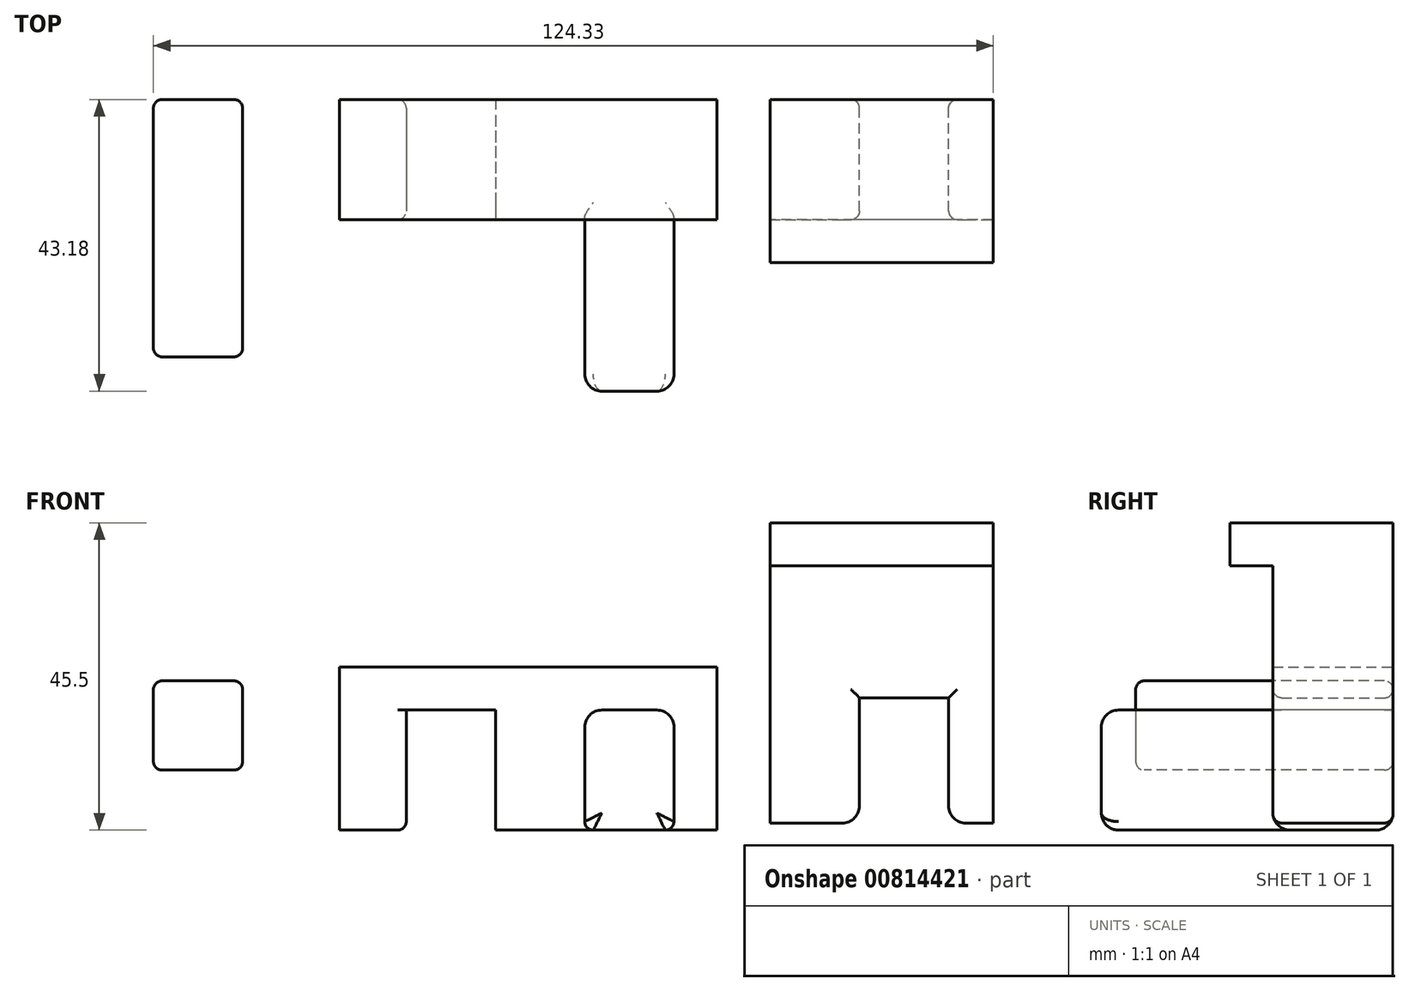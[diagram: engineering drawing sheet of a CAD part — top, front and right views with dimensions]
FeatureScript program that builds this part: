
annotation { "Feature Type Name" : "Feature", "Feature Type Description" : "" }
export const myFeature = defineFeature(function(context is Context, id is Id, definition is map)
    precondition{}
    {
        {
            var Q0;
            Q0=qCreatedBy(makeId("Front.planeOp"),FACE);
            var sketch = newSketch(context, id + "F0", { "sketchPlane" : qUnion([Q0])});
            skLineSegment(sketch, "E0.bottom", {"start": v(27.94, 8.9) * mm, "end": v(-27.94, 8.9) * mm});
            skLineSegment(sketch, "E0.top", {"start": v(27.94, -8.9) * mm, "end": v(-27.94, -8.9) * mm});
            skLineSegment(sketch, "E0.left", {"start": v(27.94, 8.9) * mm, "end": v(27.94, -8.9) * mm});
            skLineSegment(sketch, "E0.right", {"start": v(-27.94, 8.9) * mm, "end": v(-27.94, -8.9) * mm});
            skPoint(sketch, "E0.middle", {"position": v(0, 0) * mm});
            skSolve(sketch);
        }
        {
            var Q0;
            Q0=makeQuery(id+"F0.imprint","IMPRINT",FACE,{"disambiguationData":[TD([[makeQuery(id+"F0.imprint","IMPRINT",EDGE,{"derivedFrom":sQuery(id+"F0.wireOp",EDGE,"E0.bottom")}),1.0]])]});
            extrude(context, id + "F1", {"entities" : qUnion([Q0]), "depth" : 17.78 * mm, "offsetDistance" : 25.4 * mm});
        }
        {
            var Q0;
            Q0=makeQuery(id+"F1.opExtrude","CAP_FACE",FACE,{"disambiguationData":[OSD([sQuery(id+"F0.wireOp",EDGE,"E0.bottom"),sQuery(id+"F0.wireOp",EDGE,"E0.top"),sQuery(id+"F0.wireOp",EDGE,"E0.left"),sQuery(id+"F0.wireOp",EDGE,"E0.right")])],"isStart":false});
            var sketch = newSketch(context, id + "F2", { "sketchPlane" : qUnion([Q0])});
            skLineSegment(sketch, "E1.bottom", {"start": v(-18.03, 8.9) * mm, "end": v(-4.83, 8.9) * mm});
            skLineSegment(sketch, "E1.top", {"start": v(-18.03, -8.9) * mm, "end": v(-4.83, -8.9) * mm});
            skLineSegment(sketch, "E1.left", {"start": v(-18.03, 8.9) * mm, "end": v(-18.03, -8.9) * mm});
            skLineSegment(sketch, "E1.right", {"start": v(-4.83, 8.9) * mm, "end": v(-4.83, -8.9) * mm});
            skLineSegment(sketch, "E2.bottom", {"start": v(21.59, 8.9) * mm, "end": v(8.38, 8.9) * mm});
            skLineSegment(sketch, "E2.top", {"start": v(21.6, -8.9) * mm, "end": v(8.38, -8.9) * mm});
            skLineSegment(sketch, "E2.left", {"start": v(21.59, 8.9) * mm, "end": v(21.6, -8.9) * mm});
            skLineSegment(sketch, "E2.right", {"start": v(8.38, 8.9) * mm, "end": v(8.38, -8.9) * mm});
            skSolve(sketch);
        }
        {
            var Q0;
            Q0=makeQuery(id+"F2.imprint","IMPRINT",FACE,{"disambiguationData":[TD([[makeQuery(id+"F2.imprint","IMPRINT",EDGE,{"derivedFrom":sQuery(id+"F2.wireOp",EDGE,"E2.bottom")}),1.0]])]});
            extrude(context, id + "F3", {"entities" : qUnion([Q0]), "operationType" : NewBodyOperationType.ADD, "depth" : 25.4 * mm, "offsetDistance" : 25.4 * mm});
        }
        {
            var Q0;
            Q0=makeQuery(id+"F2.imprint","IMPRINT",FACE,{"disambiguationData":[TD([[makeQuery(id+"F2.imprint","IMPRINT",EDGE,{"derivedFrom":sQuery(id+"F2.wireOp",EDGE,"E1.bottom")}),1.0]])]});
            extrude(context, id + "F4", {"entities" : qUnion([Q0]), "operationType" : NewBodyOperationType.REMOVE, "endBound" : BoundingType.UP_TO_NEXT, "oppositeDirection" : true, "depth" : 25.4 * mm, "offsetDistance" : 25.4 * mm});
        }
        {
            var Q0;
            {var subQ2=sQuery(id+"F2.wireOp",EDGE,"E2.bottom");var subQ3=sQuery(id+"F0.wireOp",EDGE,"E0.left");var subQ6=sQuery(id+"F0.wireOp",EDGE,"E0.bottom");Q0=makeQuery(id+"F4.boolean.opBoolean","SPLIT",FACE,{"disambiguationData":[TD([makeQuery(id+"F1.opExtrude","SWEPT_FACE",FACE,{"disambiguationData":[OSD([subQ3])]})])],"derivedFrom":makeQuery(id+"F3.boolean.opBoolean","MERGE",FACE,{"derivedFrom":[makeQuery(id+"F1.opExtrude","SWEPT_FACE",FACE,{"disambiguationData":[OSD([subQ6])]}),makeQuery(id+"F3.opExtrude","SWEPT_FACE",FACE,{"disambiguationData":[OSD([subQ2])]})]})});}
            var sketch = newSketch(context, id + "F5", { "sketchPlane" : qUnion([Q0])});
            skLineSegment(sketch, "E3.bottom", {"start": v(27.94, 0) * mm, "end": v(-27.94, 0) * mm});
            skLineSegment(sketch, "E3.top", {"start": v(27.94, -17.78) * mm, "end": v(-27.94, -17.78) * mm});
            skLineSegment(sketch, "E3.left", {"start": v(27.94, 0) * mm, "end": v(27.94, -17.78) * mm});
            skLineSegment(sketch, "E3.right", {"start": v(-27.94, 0) * mm, "end": v(-27.94, -17.78) * mm});
            skSolve(sketch);
        }
        {
            var Q0;
            {var subQ6=sQuery(id+"F5.wireOp",EDGE,"E3.left");Q0=makeQuery(id+"F5.imprint","IMPRINT",FACE,{"disambiguationData":[TD([[makeQuery(id+"F5.imprint","IMPRINT",EDGE,{"derivedFrom":subQ6}),1.0]])]});}
            var Q1;
            {var subQ2=sQuery(id+"F5.wireOp",EDGE,"E3.right");Q1=makeQuery(id+"F5.imprint","IMPRINT",FACE,{"disambiguationData":[TD([[makeQuery(id+"F5.imprint","IMPRINT",EDGE,{"derivedFrom":subQ2}),1.0]])]});}
            extrude(context, id + "F6", {"entities" : qUnion([Q0, Q1]), "operationType" : NewBodyOperationType.ADD, "depth" : 6.35 * mm, "offsetDistance" : 25.4 * mm});
        }
        {
            var Q0;
            Q0=makeQuery(id+"F3.opExtrude","SWEPT_EDGE",EDGE,{"disambiguationData":[OSD([sQuery(id+"F0.wireOp",EDGE,"E0.bottom"),sQuery(id+"F2.wireOp",EDGE,"E2.bottom"),sQuery(id+"F2.wireOp",EDGE,"E2.left")])]});
            var Q1;
            Q1=makeQuery(id+"F3.opExtrude","CAP_EDGE",EDGE,{"disambiguationData":[OSD([sQuery(id+"F2.wireOp",EDGE,"E2.bottom")])],"isStart":false});
            var Q2;
            Q2=makeQuery(id+"F3.opExtrude","SWEPT_EDGE",EDGE,{"disambiguationData":[OSD([sQuery(id+"F0.wireOp",EDGE,"E0.bottom"),sQuery(id+"F2.wireOp",EDGE,"E2.bottom"),sQuery(id+"F2.wireOp",EDGE,"E2.right")])]});
            var Q3;
            Q3=makeQuery(id+"F3.opExtrude","CAP_EDGE",EDGE,{"disambiguationData":[OSD([sQuery(id+"F2.wireOp",EDGE,"E2.right")])],"isStart":false});
            var Q4;
            Q4=makeQuery(id+"F3.opExtrude","CAP_EDGE",EDGE,{"disambiguationData":[OSD([sQuery(id+"F2.wireOp",EDGE,"E2.left")])],"isStart":false});
            var Q5;
            Q5=makeQuery(id+"F3.opExtrude","CAP_EDGE",EDGE,{"disambiguationData":[OSD([sQuery(id+"F2.wireOp",EDGE,"E2.top")])],"isStart":false});
            var Q6;
            {var subQ1=makeQuery(id+"F3.opExtrude","SWEPT_FACE",FACE,{"disambiguationData":[OSD([sQuery(id+"F2.wireOp",EDGE,"E2.right")])]});var subQ2=sQuery(id+"F0.wireOp",EDGE,"E0.top");var subQ4=sQuery(id+"F0.wireOp",EDGE,"E0.right");Q6=makeQuery(id+"F4.boolean.opBoolean","SPLIT",EDGE,{"disambiguationData":[TD([subQ1])],"derivedFrom":makeQuery(id+"F3.boolean.opBoolean","SPLIT",EDGE,{"disambiguationData":[TD([makeQuery(id+"F1.opExtrude","SWEPT_FACE",FACE,{"disambiguationData":[OSD([subQ4])]})])],"derivedFrom":makeQuery(id+"F1.opExtrude","CAP_EDGE",EDGE,{"disambiguationData":[OSD([subQ2])],"isStart":false})})});}
            var Q7;
            {var subQ0=sQuery(id+"F0.wireOp",EDGE,"E0.left");var subQ1=sQuery(id+"F0.wireOp",EDGE,"E0.top");Q7=makeQuery(id+"F3.boolean.opBoolean","SPLIT",EDGE,{"disambiguationData":[TD([makeQuery(id+"F1.opExtrude","SWEPT_FACE",FACE,{"disambiguationData":[OSD([subQ0])]})])],"derivedFrom":makeQuery(id+"F1.opExtrude","CAP_EDGE",EDGE,{"disambiguationData":[OSD([subQ1])],"isStart":false})});}
            var Q8;
            {var subQ1=sQuery(id+"F0.wireOp",EDGE,"E0.right");var subQ2=makeQuery(id+"F1.opExtrude","SWEPT_FACE",FACE,{"disambiguationData":[OSD([subQ1])]});var subQ3=sQuery(id+"F0.wireOp",EDGE,"E0.top");Q8=makeQuery(id+"F4.boolean.opBoolean","SPLIT",EDGE,{"disambiguationData":[TD([subQ2])],"derivedFrom":makeQuery(id+"F3.boolean.opBoolean","SPLIT",EDGE,{"disambiguationData":[TD([subQ2])],"derivedFrom":makeQuery(id+"F1.opExtrude","CAP_EDGE",EDGE,{"disambiguationData":[OSD([subQ3])],"isStart":false})})});}
            var Q9;
            {var subQ0=sQuery(id+"F0.wireOp",EDGE,"E0.left");var subQ1=sQuery(id+"F0.wireOp",EDGE,"E0.top");Q9=makeQuery(id+"F4.boolean.opBoolean","SPLIT",EDGE,{"disambiguationData":[TD([makeQuery(id+"F1.opExtrude","SWEPT_FACE",FACE,{"disambiguationData":[OSD([subQ0])]})])],"derivedFrom":makeQuery(id+"F1.opExtrude","CAP_EDGE",EDGE,{"disambiguationData":[OSD([subQ1])],"isStart":true})});}
            var Q10;
            {var subQ0=sQuery(id+"F0.wireOp",EDGE,"E0.right");var subQ1=sQuery(id+"F0.wireOp",EDGE,"E0.top");Q10=makeQuery(id+"F4.boolean.opBoolean","SPLIT",EDGE,{"disambiguationData":[TD([makeQuery(id+"F1.opExtrude","SWEPT_FACE",FACE,{"disambiguationData":[OSD([subQ0])]})])],"derivedFrom":makeQuery(id+"F1.opExtrude","CAP_EDGE",EDGE,{"disambiguationData":[OSD([subQ1])],"isStart":true})});}
            fillet(context, id + "F7", {"entities" : qUnion([Q0, Q1, Q2, Q3, Q4, Q5, Q6, Q7, Q8, Q9, Q10]), "radius" : 2.54 * mm, "tangentPropagation" : true, "allowEdgeOverflow" : false});
        }
        {
            var Q0;
            Q0=qCreatedBy(makeId("Top.planeOp"),FACE);
            var sketch = newSketch(context, id + "F8", { "sketchPlane" : qUnion([Q0])});
            skLineSegment(sketch, "E4.bottom", {"start": v(-55.47, 0) * mm, "end": v(-42.26, 0) * mm});
            skLineSegment(sketch, "E4.top", {"start": v(-55.47, -38.1) * mm, "end": v(-42.26, -38.1) * mm});
            skLineSegment(sketch, "E4.left", {"start": v(-55.47, 0) * mm, "end": v(-55.47, -38.1) * mm});
            skLineSegment(sketch, "E4.right", {"start": v(-42.26, 0) * mm, "end": v(-42.26, -38.1) * mm});
            skSolve(sketch);
        }
        {
            var Q0;
            Q0=makeQuery(id+"F8.imprint","IMPRINT",FACE,{"disambiguationData":[TD([[makeQuery(id+"F8.imprint","IMPRINT",EDGE,{"derivedFrom":sQuery(id+"F8.wireOp",EDGE,"E4.bottom")}),-1.0]])]});
            extrude(context, id + "F9", {"entities" : qUnion([Q0]), "depth" : 13.2 * mm, "offsetDistance" : 25.4 * mm});
        }
        {
            var Q0;
            Q0=makeQuery(id+"F9.opExtrude","CAP_EDGE",EDGE,{"disambiguationData":[OSD([sQuery(id+"F8.wireOp",EDGE,"E4.left")])],"isStart":false});
            var Q1;
            Q1=makeQuery(id+"F9.opExtrude","CAP_EDGE",EDGE,{"disambiguationData":[OSD([sQuery(id+"F8.wireOp",EDGE,"E4.right")])],"isStart":true});
            var Q2;
            Q2=makeQuery(id+"F9.opExtrude","CAP_EDGE",EDGE,{"disambiguationData":[OSD([sQuery(id+"F8.wireOp",EDGE,"E4.right")])],"isStart":false});
            var Q3;
            Q3=makeQuery(id+"F9.opExtrude","CAP_EDGE",EDGE,{"disambiguationData":[OSD([sQuery(id+"F8.wireOp",EDGE,"E4.left")])],"isStart":true});
            var Q4;
            Q4=makeQuery(id+"F9.opExtrude","SWEPT_FACE",FACE,{"disambiguationData":[OSD([sQuery(id+"F8.wireOp",EDGE,"E4.top")])]});
            var Q5;
            Q5=makeQuery(id+"F9.opExtrude","SWEPT_FACE",FACE,{"disambiguationData":[OSD([sQuery(id+"F8.wireOp",EDGE,"E4.bottom")])]});
            fillet(context, id + "F10", {"entities" : qUnion([Q0, Q1, Q2, Q3, Q4, Q5]), "radius" : 1.27 * mm, "tangentPropagation" : true, "allowEdgeOverflow" : false});
        }
        {
            var Q0;
            Q0=qCreatedBy(makeId("Front.planeOp"),FACE);
            var sketch = newSketch(context, id + "F11", { "sketchPlane" : qUnion([Q0])});
            skLineSegment(sketch, "E5.bottom", {"start": v(35.84, 36.6) * mm, "end": v(68.86, 36.6) * mm});
            skLineSegment(sketch, "E5.top", {"start": v(35.84, -7.84) * mm, "end": v(68.86, -7.84) * mm});
            skLineSegment(sketch, "E5.left", {"start": v(35.84, 36.6) * mm, "end": v(35.84, -7.84) * mm});
            skLineSegment(sketch, "E5.right", {"start": v(68.86, 36.6) * mm, "end": v(68.86, -7.84) * mm});
            skLineSegment(sketch, "E6.bottom", {"start": v(62.25, -7.84) * mm, "end": v(49.04, -7.84) * mm});
            skLineSegment(sketch, "E6.top", {"start": v(62.25, 10.7) * mm, "end": v(49.04, 10.7) * mm});
            skLineSegment(sketch, "E6.left", {"start": v(62.25, -7.84) * mm, "end": v(62.25, 10.7) * mm});
            skLineSegment(sketch, "E6.right", {"start": v(49.04, -7.84) * mm, "end": v(49.04, 10.7) * mm});
            skSolve(sketch);
        }
        {
            var Q0;
            Q0=makeQuery(id+"F11.imprint","IMPRINT",FACE,{"disambiguationData":[TD([[makeQuery(id+"F11.imprint","IMPRINT",EDGE,{"derivedFrom":sQuery(id+"F11.wireOp",EDGE,"E5.bottom")}),-1.0]])]});
            extrude(context, id + "F12", {"entities" : qUnion([Q0]), "depth" : 17.78 * mm, "offsetDistance" : 25.4 * mm});
        }
        {
            var Q0;
            Q0=makeQuery(id+"F12.opExtrude","SWEPT_EDGE",EDGE,{"disambiguationData":[OSD([sQuery(id+"F11.wireOp",EDGE,"E5.top"),sQuery(id+"F11.wireOp",EDGE,"E6.bottom"),sQuery(id+"F11.wireOp",EDGE,"E6.right")])]});
            var Q1;
            Q1=makeQuery(id+"F12.opExtrude","SWEPT_EDGE",EDGE,{"disambiguationData":[OSD([sQuery(id+"F11.wireOp",EDGE,"E5.top"),sQuery(id+"F11.wireOp",EDGE,"E6.bottom"),sQuery(id+"F11.wireOp",EDGE,"E6.left")])]});
            fillet(context, id + "F13", {"entities" : qUnion([Q0, Q1]), "radius" : 2.54 * mm, "tangentPropagation" : true, "allowEdgeOverflow" : false});
        }
        {
            var Q0;
            Q0=makeQuery(id+"F12.opExtrude","CAP_FACE",FACE,{"disambiguationData":[OSD([sQuery(id+"F11.wireOp",EDGE,"E5.bottom"),sQuery(id+"F11.wireOp",EDGE,"E5.top"),sQuery(id+"F11.wireOp",EDGE,"E5.left"),sQuery(id+"F11.wireOp",EDGE,"E5.right"),sQuery(id+"F11.wireOp",EDGE,"E6.top"),sQuery(id+"F11.wireOp",EDGE,"E6.left"),sQuery(id+"F11.wireOp",EDGE,"E6.right")])],"isStart":false});
            var sketch = newSketch(context, id + "F14", { "sketchPlane" : qUnion([Q0])});
            skLineSegment(sketch, "E7.bottom", {"start": v(68.86, 36.6) * mm, "end": v(35.84, 36.6) * mm});
            skLineSegment(sketch, "E7.top", {"start": v(68.86, 30.26) * mm, "end": v(35.84, 30.26) * mm});
            skLineSegment(sketch, "E7.left", {"start": v(68.86, 36.6) * mm, "end": v(68.86, 30.26) * mm});
            skLineSegment(sketch, "E7.right", {"start": v(35.84, 36.6) * mm, "end": v(35.84, 30.26) * mm});
            skSolve(sketch);
        }
        {
            var Q0;
            Q0=makeQuery(id+"F14.imprint","IMPRINT",FACE,{"disambiguationData":[TD([[makeQuery(id+"F14.imprint","IMPRINT",EDGE,{"derivedFrom":sQuery(id+"F14.wireOp",EDGE,"E7.bottom")}),-1.0]])]});
            extrude(context, id + "F15", {"entities" : qUnion([Q0]), "operationType" : NewBodyOperationType.ADD, "depth" : 6.35 * mm, "offsetDistance" : 25.4 * mm});
        }
        {
            var Q0;
            Q0=makeQuery(id+"F4.boolean.opBoolean","COPY",EDGE,{"derivedFrom":makeQuery(id+"F4.opExtrude","SWEPT_EDGE",EDGE,{"disambiguationData":[OSD([sQuery(id+"F0.wireOp",EDGE,"E0.top"),sQuery(id+"F2.wireOp",EDGE,"E1.top"),sQuery(id+"F2.wireOp",EDGE,"E1.left")])]})});
            var Q1;
            Q1=makeQuery(id+"F4.boolean.opBoolean","COPY",EDGE,{"derivedFrom":makeQuery(id+"F4.opExtrude","SWEPT_EDGE",EDGE,{"disambiguationData":[OSD([sQuery(id+"F0.wireOp",EDGE,"E0.top"),sQuery(id+"F2.wireOp",EDGE,"E1.top"),sQuery(id+"F2.wireOp",EDGE,"E1.right")])]})});
            var Q2;
            Q2=makeQuery(id+"F3.opExtrude","SWEPT_EDGE",EDGE,{"disambiguationData":[OSD([sQuery(id+"F0.wireOp",EDGE,"E0.top"),sQuery(id+"F2.wireOp",EDGE,"E2.top"),sQuery(id+"F2.wireOp",EDGE,"E2.right")])]});
            var Q3;
            Q3=makeQuery(id+"F3.opExtrude","SWEPT_EDGE",EDGE,{"disambiguationData":[OSD([sQuery(id+"F0.wireOp",EDGE,"E0.top"),sQuery(id+"F2.wireOp",EDGE,"E2.top"),sQuery(id+"F2.wireOp",EDGE,"E2.left")])]});
            var Q4;
            Q4=makeQuery(id+"F12.opExtrude","CAP_EDGE",EDGE,{"disambiguationData":[OSD([sQuery(id+"F11.wireOp",EDGE,"E6.right")])],"isStart":true});
            var Q5;
            Q5=makeQuery(id+"F12.opExtrude","CAP_EDGE",EDGE,{"disambiguationData":[OSD([sQuery(id+"F11.wireOp",EDGE,"E6.top")])],"isStart":true});
            var Q6;
            Q6=makeQuery(id+"F12.opExtrude","CAP_EDGE",EDGE,{"disambiguationData":[OSD([sQuery(id+"F11.wireOp",EDGE,"E6.left")])],"isStart":true});
            var Q7;
            Q7=makeQuery(id+"F12.opExtrude","CAP_EDGE",EDGE,{"disambiguationData":[OSD([sQuery(id+"F11.wireOp",EDGE,"E6.left")])],"isStart":false});
            var Q8;
            Q8=makeQuery(id+"F12.opExtrude","CAP_EDGE",EDGE,{"disambiguationData":[OSD([sQuery(id+"F11.wireOp",EDGE,"E6.top")])],"isStart":false});
            var Q9;
            Q9=makeQuery(id+"F12.opExtrude","CAP_EDGE",EDGE,{"disambiguationData":[OSD([sQuery(id+"F11.wireOp",EDGE,"E6.right")])],"isStart":false});
            fillet(context, id + "F16", {"entities" : qUnion([Q0, Q1, Q2, Q3, Q4, Q5, Q6, Q7, Q8, Q9]), "radius" : 1.27 * mm, "tangentPropagation" : true, "allowEdgeOverflow" : false});
        }
    });
